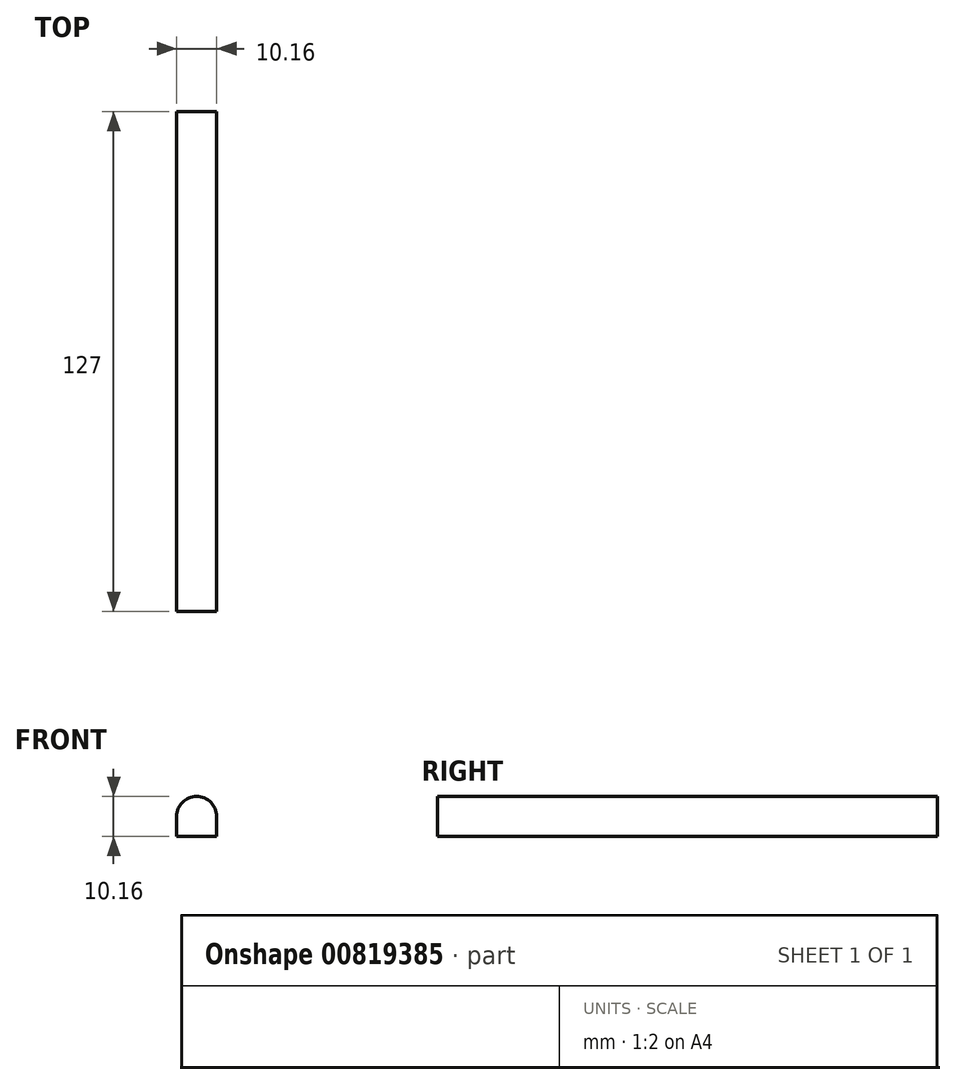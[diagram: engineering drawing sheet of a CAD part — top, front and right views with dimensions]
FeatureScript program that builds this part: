
annotation { "Feature Type Name" : "Feature", "Feature Type Description" : "" }
export const myFeature = defineFeature(function(context is Context, id is Id, definition is map)
    precondition{}
    {
        {
            var Q0;
            Q0=qCreatedBy(makeId("Front.planeOp"),FACE);
            var sketch = newSketch(context, id + "F0", { "sketchPlane" : qUnion([Q0])});
            skLineSegment(sketch, "E0", {"start": v(0, 5.08) * mm, "end": v(0, 0) * mm});
            skLineSegment(sketch, "E1", {"start": v(0, 0) * mm, "end": v(10.16, 0) * mm});
            skLineSegment(sketch, "E2", {"start": v(10.16, 0) * mm, "end": v(10.16, 5.08) * mm});
            skArc(sketch, "E3", {"start": v(10.16, 5.08) * mm, "mid": v(5.08, 10.16) * mm, "end": v(0, 5.08) * mm});
            skSolve(sketch);
        }
        {
            var Q0;
            Q0=qSketchRegion(id+"F0",true);
            extrude(context, id + "F1", {"entities" : qUnion([Q0]), "depth" : 127 * mm, "offsetDistance" : 25.4 * mm});
        }
    });
